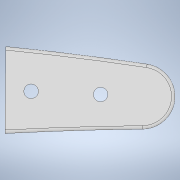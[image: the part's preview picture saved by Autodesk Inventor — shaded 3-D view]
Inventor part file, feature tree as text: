
AUTODESK INVENTOR PART (.ipt)
format: ipt  version: 2020.3 (Build 243373000, 373)  size: 204,800 bytes
history: native  units: mm
features: sketch x1, extrude x1, shell x1, hole x1, fillet x1
ambient origin geometry x8: Origin, YZ Plane, XZ Plane, XY Plane, X Axis, Y Axis, Z Axis, Center Point
bodies: Body1 (feature_tree)
feature tree (5):
  sketch  "Sketch1"  dims[d4=6.0mm d5=24.6mm d6=12.4mm d7=6.0mm d15=7.0mm d17=9.0mm d21=20.0mm d23=80.0mm d24=20.0mm d29=29.670597mm d30=6.0mm d31=10.0mm d43=4.0mm d44=3.0mm d45=4.0mm d50=13.0mm d51=12.0mm d52=22.68928mm d89=6.8mm d90=28.4mm d107=420.0mm d108=4.0mm d109=4.0mm d114=1.2mm d115=1.2mm d116=8.4mm d117=0.0mm d118=1.0mm d119=2.1mm d120=6.0mm d121=4.0mm d122=2.0mm d123=90.0deg d124=8.0mm d125=20.594885mm d126=0.5mm]
  extrude  "Extrusion4"  Depth=0.5mm
  shell  "Shell1"  Thickness=12.4mm
  hole  "Hole6"  [1 undecoded]
  fillet  "Fillet12"  Radius=7.0mm
note: 1 required parameter value undecoded (feature->parameter linkage not recoverable at this tier; creation-order binding heuristic only, values carry confidence <= 0.55)
